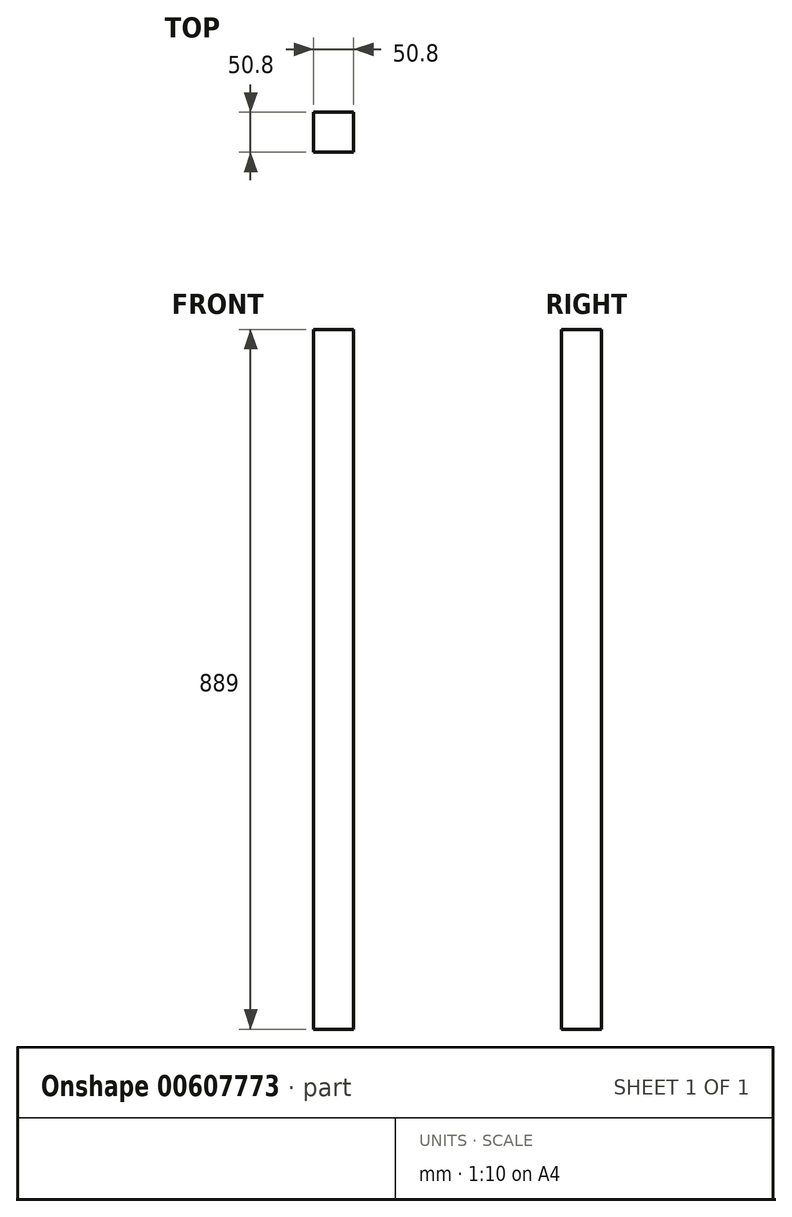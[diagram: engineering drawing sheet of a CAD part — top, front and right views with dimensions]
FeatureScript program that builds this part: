
annotation { "Feature Type Name" : "Feature", "Feature Type Description" : "" }
export const myFeature = defineFeature(function(context is Context, id is Id, definition is map)
    precondition{}
    {
        {
            var Q0;
            Q0=qCreatedBy(makeId("Front.planeOp"),FACE);
            var sketch = newSketch(context, id + "F0", { "sketchPlane" : qUnion([Q0])});
            skLineSegment(sketch, "E0.bottom", {"start": v(0, 0) * mm, "end": v(-50.8, 0) * mm});
            skLineSegment(sketch, "E0.top", {"start": v(0, 889) * mm, "end": v(-50.8, 889) * mm});
            skLineSegment(sketch, "E0.left", {"start": v(0, 0) * mm, "end": v(0, 889) * mm});
            skLineSegment(sketch, "E0.right", {"start": v(-50.8, 0) * mm, "end": v(-50.8, 889) * mm});
            skSolve(sketch);
        }
        {
            var Q0;
            Q0=makeQuery(id+"F0.imprint","IMPRINT",FACE,{"disambiguationData":[TD([[makeQuery(id+"F0.imprint","IMPRINT",EDGE,{"derivedFrom":sQuery(id+"F0.wireOp",EDGE,"E0.bottom")}),-1.0]])]});
            extrude(context, id + "F1", {"entities" : qUnion([Q0]), "depth" : 50.8 * mm, "offsetDistance" : 25.4 * mm});
        }
    });
